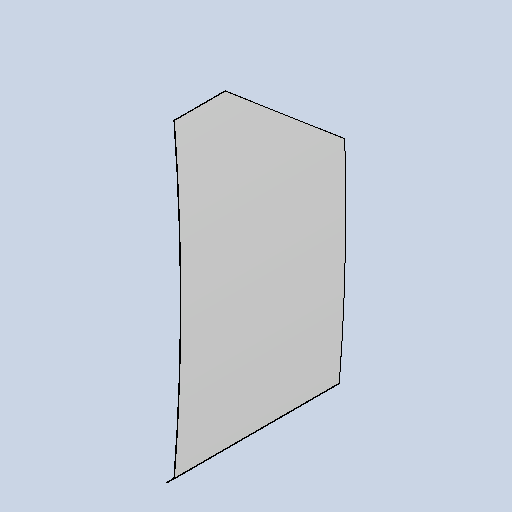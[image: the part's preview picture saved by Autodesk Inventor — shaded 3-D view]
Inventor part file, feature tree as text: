
AUTODESK INVENTOR PART (.ipt)
format: ipt  version: 2025 (Build 290162010, 162A)  size: 342,528 bytes
history: native  units: mm
features: other x4, sheet_metal_op x3, sketch x3, extrude x1, projected_geometry x1
ambient origin geometry x8: Origin, YZ Plane, XZ Plane, XY Plane, X Axis, Y Axis, Z Axis, Center Point
bodies: Body1 (feature_tree)
feature tree (12):
  sheet_metal_op  "Contour Flange2"
  extrude  "Extrusion2"  Depth=3.0mm
  other  "Mark5"
  other  "A-Side Definition"
  sketch  "Sketch1"  dims[d36=3.0mm d37=3.0mm]
  other  "Plate2"
  sheet_metal_op  "Bend2"
  sheet_metal_op  "Corner2"
  sketch  "Sketch2"  dims[d38=1.5mm]
  projected_geometry  "Projected Loop3"
  sketch  "Sketch6"  dims[d39=6.0mm d40=5.0mm d41=980.0mm d42=5.0mm d43=3.0mm d44=12.0mm d45=3.0mm d46=5.0mm d65=8.0mm d66=8.0mm d69=3.0mm d78=3.0mm d80=3.0mm d123=0.0mm d124=0.0mm d155=5.0mm d156=63.0mm d157=11050.0mm d158=23.736478mm d160=5.0mm d161=6.981317mm d162=304.0mm d164=304.0mm d165=6.981317mm d166=12.0mm d167=12.0mm d168=0.0mm d169=1843.0mm]
  other  "Definition1"
